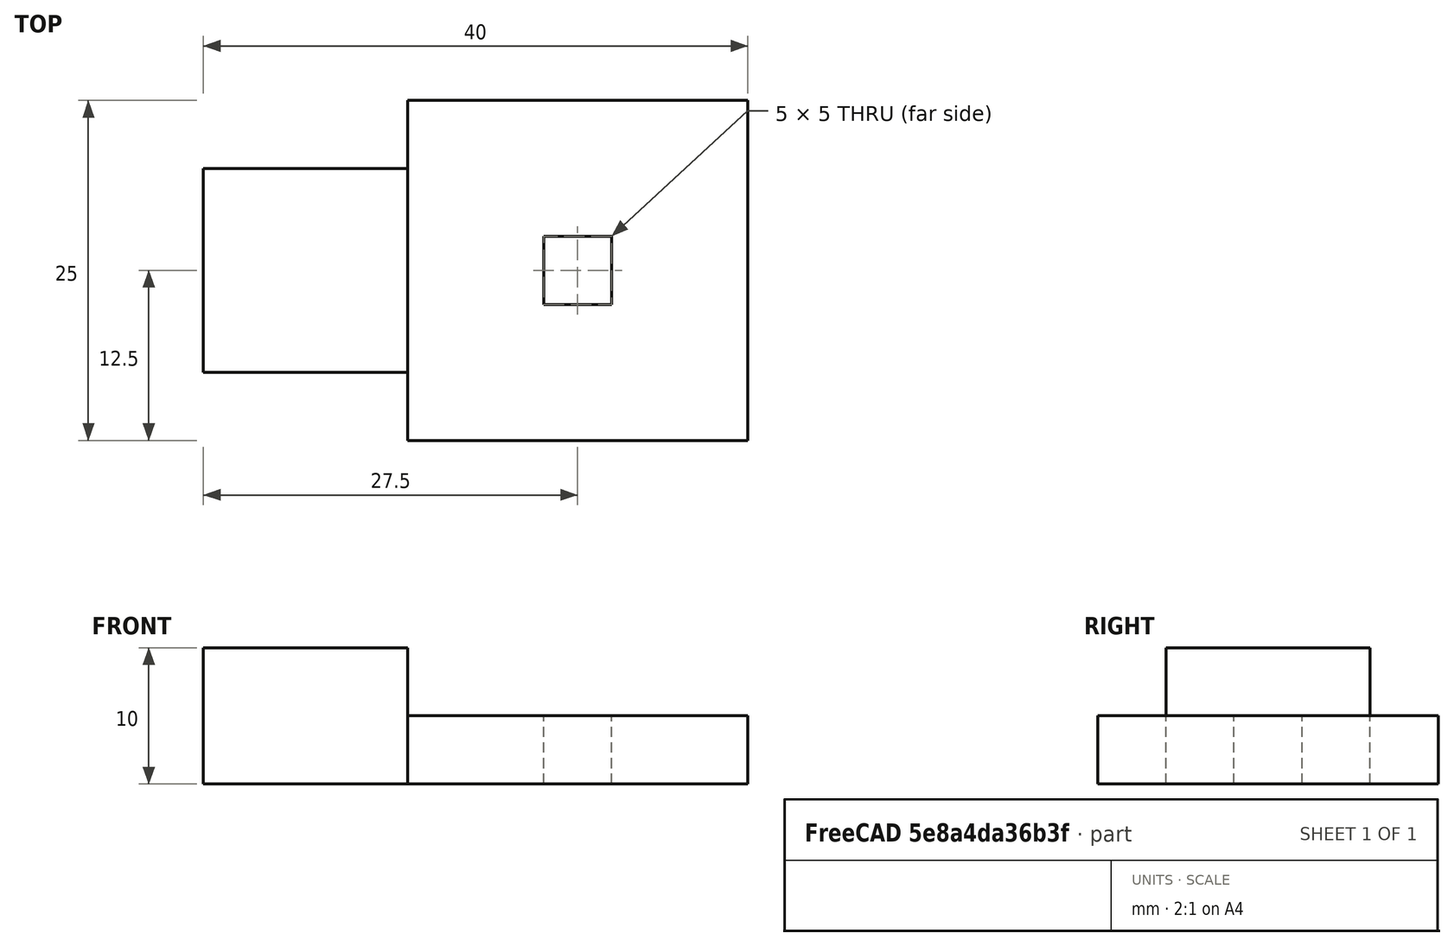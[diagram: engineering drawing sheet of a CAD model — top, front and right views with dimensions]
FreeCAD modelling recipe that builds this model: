
FCSTD DOCUMENT  (FreeCAD 0.20R25170 (Git))
Label: test_adaptive
License: All rights reserved
LicenseURL: http://en.wikipedia.org/wiki/All_rights_reserved
objects: Part::Box×3, Part::Cut×1, Part::MultiFuse×1
note: 5 computed .brp shape members not serialized (recipe doc carries the construction recipe); baked Part::Feature solids carry a one-line shape summary decoded from their .brp

FEATURE [Part::Box] Box  label="Cube"
  AttacherType = Attacher::AttachEngine3D
  Height = 10
  Length = 15
  Placement = pos=(0,5,0) rot=(0,0,1;0rad)
  Width = 15
FEATURE [Part::Box] Box001  label="Cube001"
  AttacherType = Attacher::AttachEngine3D
  Height = 5
  Length = 25
  Placement = pos=(15,0,0) rot=(0,0,1;0rad)
  Width = 25
FEATURE [Part::Box] Box002  label="Cube002"
  AttacherType = Attacher::AttachEngine3D
  Height = 10
  Length = 5
  Placement = pos=(25,10,0) rot=(0,0,1;0rad)
  Width = 5
FEATURE [Part::Cut] Cut
  Base = -> Box001
  Tool = -> Box002
FEATURE [Part::MultiFuse] Fusion
  Shapes = -> [Box,Cut]
